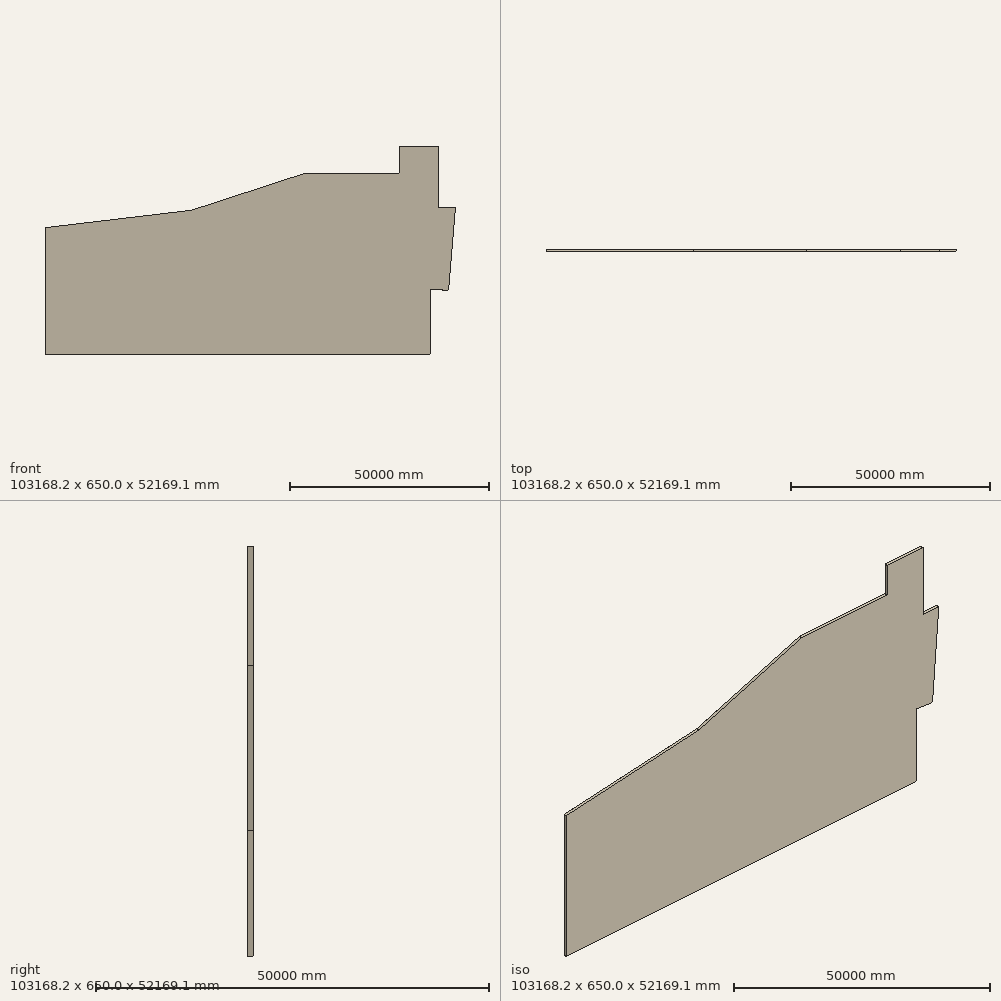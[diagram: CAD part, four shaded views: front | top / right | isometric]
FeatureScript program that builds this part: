
annotation { "Feature Type Name" : "Feature", "Feature Type Description" : "" }
export const myFeature = defineFeature(function(context is Context, id is Id, definition is map)
    precondition{}
    {
        {
            var Q0;
            Q0=qCreatedBy(makeId("Front.planeOp"),FACE);
            var sketch = newSketch(context, id + "F0", { "sketchPlane" : qUnion([Q0])});
            skLineSegment(sketch, "E0", {"start": v(0, 31823) * mm, "end": v(0, 0) * mm});
            skLineSegment(sketch, "E1", {"start": v(0, 0) * mm, "end": v(96994, 0) * mm});
            skLineSegment(sketch, "E2", {"start": v(0, 31823) * mm, "end": v(36871, 36212.16) * mm});
            skLineSegment(sketch, "E3", {"start": v(36871, 36212.16) * mm, "end": v(65304, 45473.87) * mm});
            skLineSegment(sketch, "E4", {"start": v(96994, 0) * mm, "end": v(96994, 16380) * mm});
            skPoint(sketch, "E5.end.orphan", {"position": v(65379, 52169.09) * mm});
            skPoint(sketch, "E6.end.orphan", {"position": v(91413.67, 52169.09) * mm});
            skLineSegment(sketch, "E7", {"start": v(96994, 16380) * mm, "end": v(101428, 16012.2) * mm});
            skLineSegment(sketch, "E8", {"start": v(101428, 16012.2) * mm, "end": v(103168.2, 36991.2) * mm});
            skLineSegment(sketch, "E9", {"start": v(65304, 45473.87) * mm, "end": v(88969, 45473.87) * mm});
            skLineSegment(sketch, "E10", {"start": v(88969, 45473.87) * mm, "end": v(88969, 52169.09) * mm});
            skLineSegment(sketch, "E11", {"start": v(88969, 52169.09) * mm, "end": v(98816.37, 52169.09) * mm});
            skLineSegment(sketch, "E12", {"start": v(98816.37, 52169.09) * mm, "end": v(98816.37, 36991.2) * mm});
            skLineSegment(sketch, "E13", {"start": v(98816.37, 36991.2) * mm, "end": v(103168.2, 36991.2) * mm});
            skSolve(sketch);
        }
        {
            var Q0;
            Q0=qSketchRegion(id+"F0",true);
            extrude(context, id + "F1", {"entities" : qUnion([Q0]), "depth" : 650 * mm});
        }
    });
